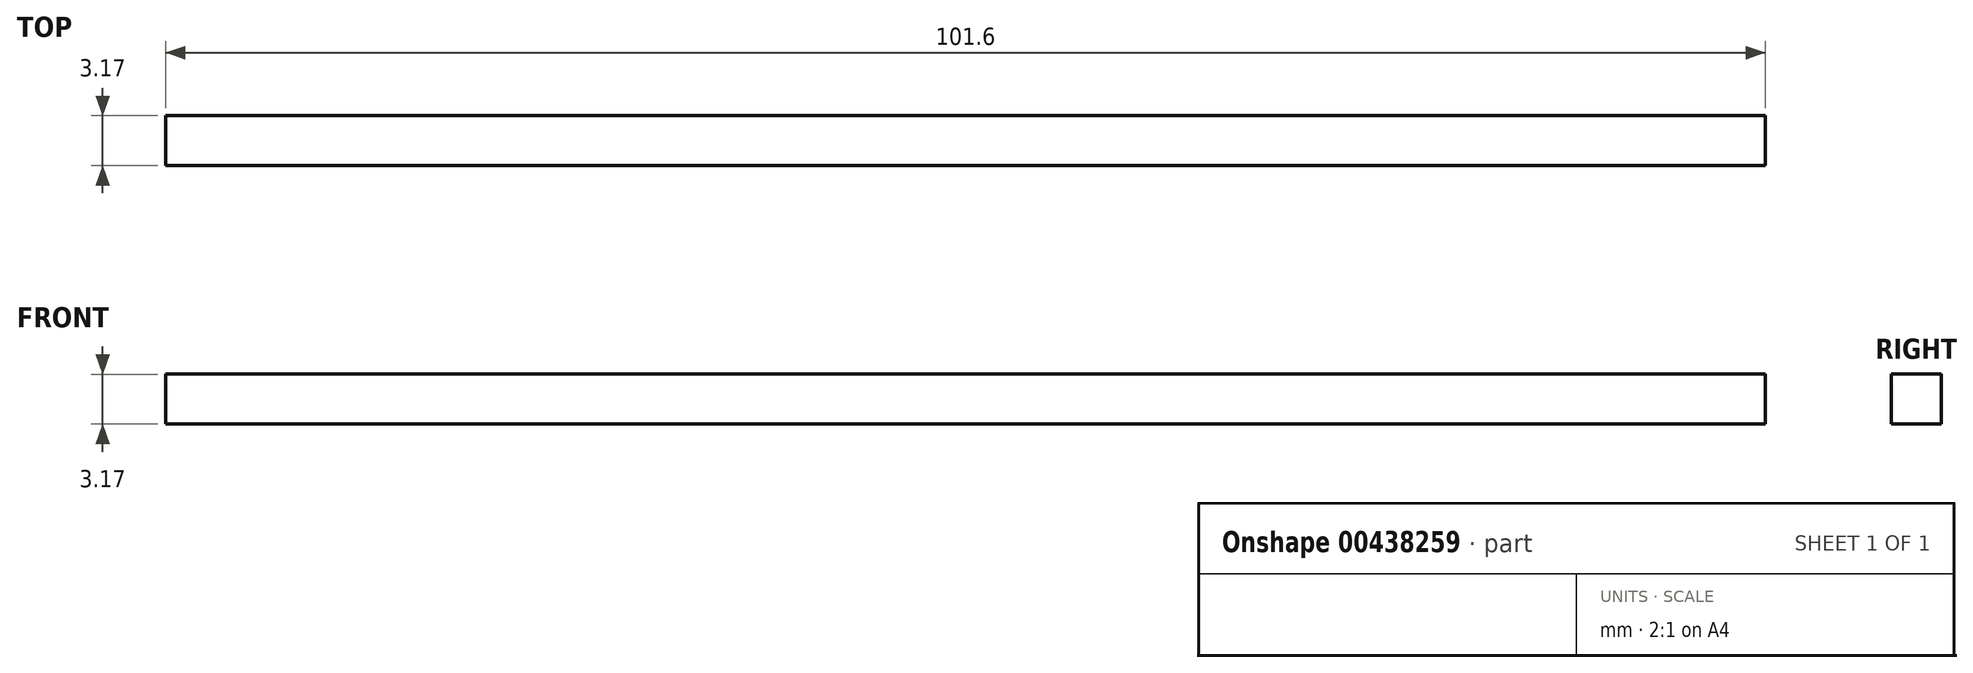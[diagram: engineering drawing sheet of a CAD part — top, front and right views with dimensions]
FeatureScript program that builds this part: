
annotation { "Feature Type Name" : "Feature", "Feature Type Description" : "" }
export const myFeature = defineFeature(function(context is Context, id is Id, definition is map)
    precondition{}
    {
        {
            var Q0;
            Q0=qCreatedBy(makeId("Top.planeOp"),FACE);
            var sketch = newSketch(context, id + "F0", { "sketchPlane" : qUnion([Q0])});
            skLineSegment(sketch, "E0.bottom", {"start": v(-51.96, 32.85) * mm, "end": v(49.64, 32.85) * mm});
            skLineSegment(sketch, "E0.top", {"start": v(-51.96, 29.68) * mm, "end": v(49.64, 29.68) * mm});
            skLineSegment(sketch, "E0.left", {"start": v(-51.96, 32.85) * mm, "end": v(-51.96, 29.68) * mm});
            skLineSegment(sketch, "E0.right", {"start": v(49.64, 32.85) * mm, "end": v(49.64, 29.68) * mm});
            skSolve(sketch);
        }
        {
            var Q0;
            Q0 = qSketchRegion(id + "F0", true);
            extrude(context, id + "F1", {"entities" : qUnion([Q0]), "depth" : 3.17 * mm});
        }
    });
